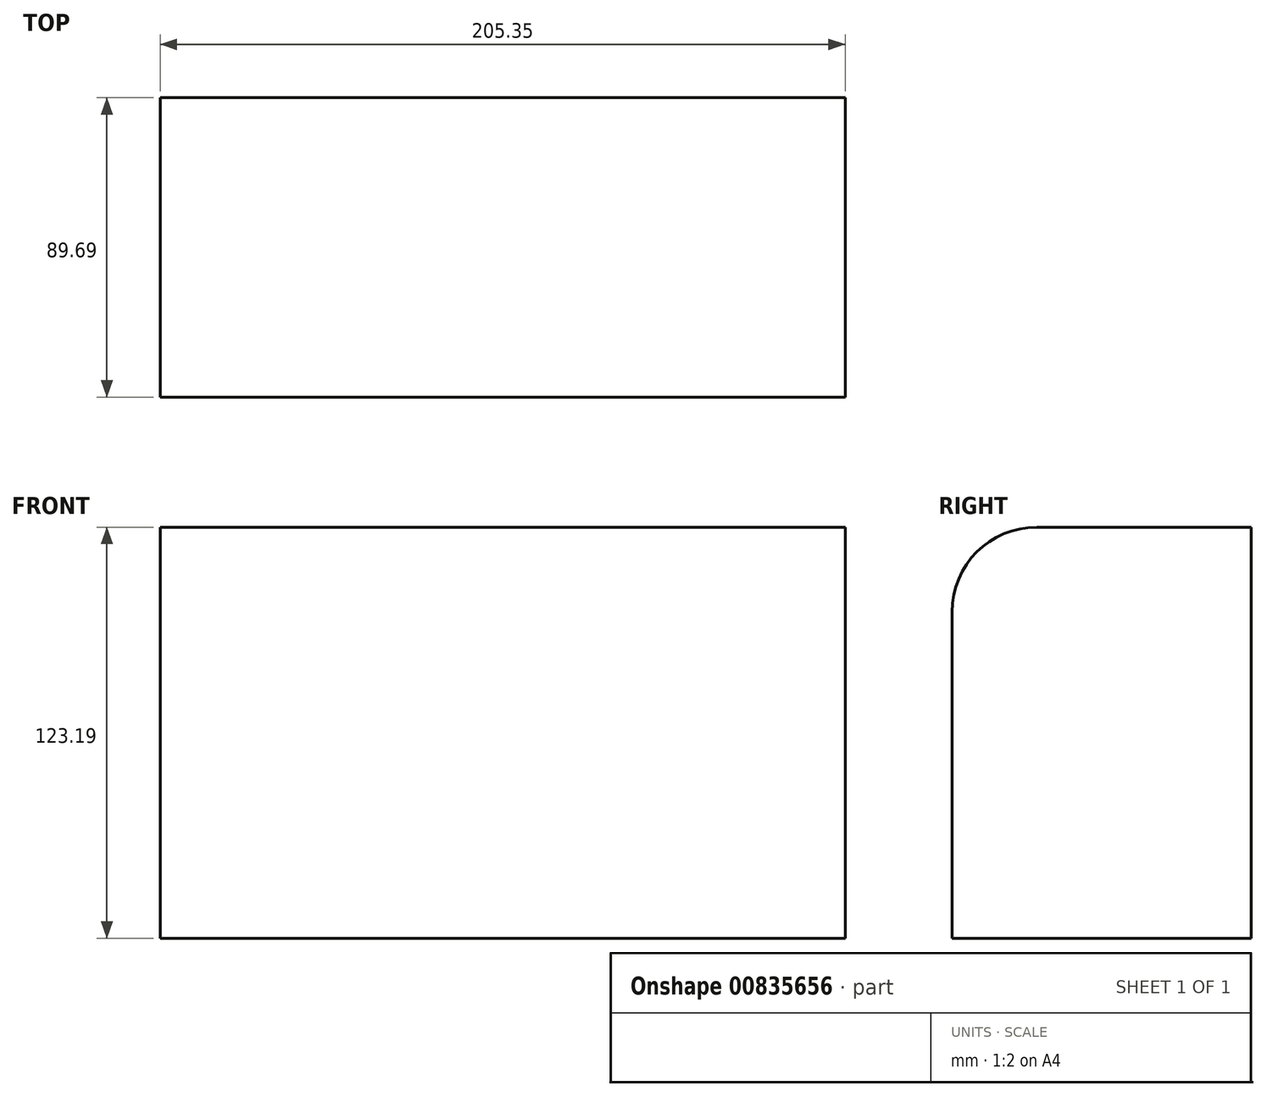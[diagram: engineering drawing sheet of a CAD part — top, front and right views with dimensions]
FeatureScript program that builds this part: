
annotation { "Feature Type Name" : "Feature", "Feature Type Description" : "" }
export const myFeature = defineFeature(function(context is Context, id is Id, definition is map)
    precondition{}
    {
        {
            var Q0;
            Q0=qCreatedBy(makeId("Top.planeOp"),FACE);
            var sketch = newSketch(context, id + "F0", { "sketchPlane" : qUnion([Q0])});
            skLineSegment(sketch, "E0.bottom", {"start": v(-122.3, 48.97) * mm, "end": v(83.06, 48.97) * mm});
            skLineSegment(sketch, "E0.top", {"start": v(-122.3, -40.72) * mm, "end": v(83.06, -40.72) * mm});
            skLineSegment(sketch, "E0.left", {"start": v(-122.3, 48.97) * mm, "end": v(-122.3, -40.72) * mm});
            skLineSegment(sketch, "E0.right", {"start": v(83.06, 48.97) * mm, "end": v(83.06, -40.72) * mm});
            skSolve(sketch);
        }
        {
            var Q0;
            Q0=makeQuery(id+"F0.imprint","IMPRINT",FACE,{"disambiguationData":[TD([[makeQuery(id+"F0.imprint","IMPRINT",EDGE,{"derivedFrom":sQuery(id+"F0.wireOp",EDGE,"E0.bottom")}),-1.0]])]});
            extrude(context, id + "F1", {"entities" : qUnion([Q0]), "depth" : 97.8 * mm, "offsetDistance" : 25.4 * mm, "hasSecondDirection" : true, "secondDirectionOppositeDirection" : true, "secondDirectionDepth" : 25.4 * mm});
        }
        {
            var Q0;
            Q0=makeQuery(id+"F1.opExtrude","CAP_EDGE",EDGE,{"disambiguationData":[OSD([sQuery(id+"F0.wireOp",EDGE,"E0.top")])],"isStart":false});
            fillet(context, id + "F2", {"entities" : qUnion([Q0]), "radius" : 25.4 * mm, "tangentPropagation" : true, "allowEdgeOverflow" : false});
        }
    });
